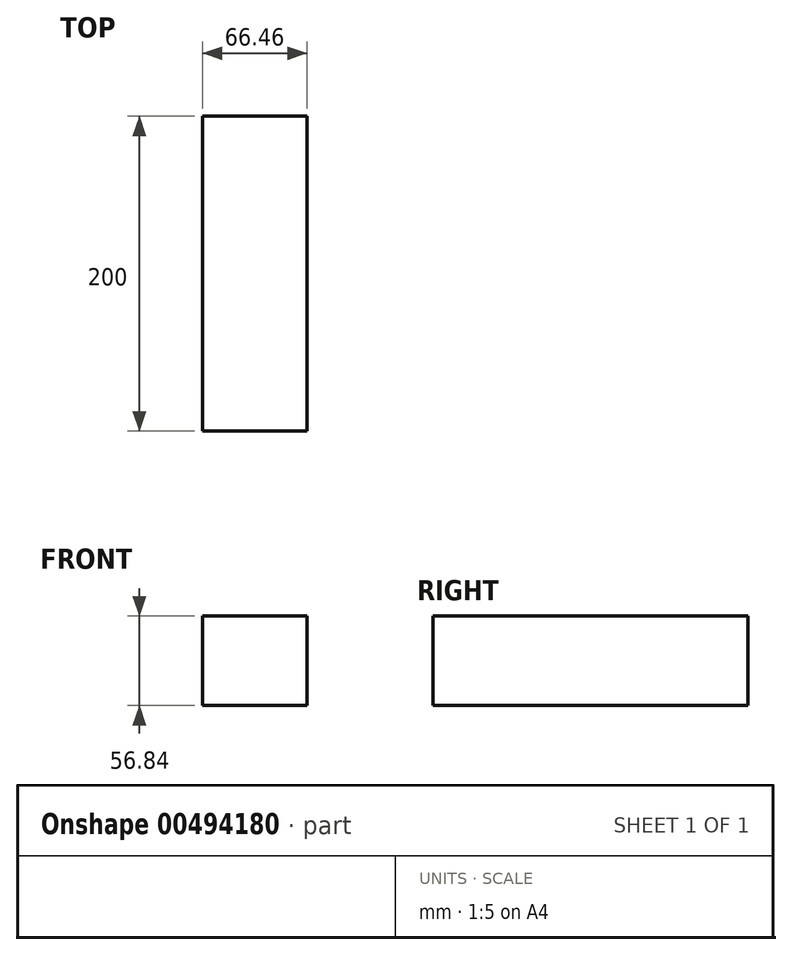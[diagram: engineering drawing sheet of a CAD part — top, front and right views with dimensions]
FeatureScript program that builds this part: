
annotation { "Feature Type Name" : "Feature", "Feature Type Description" : "" }
export const myFeature = defineFeature(function(context is Context, id is Id, definition is map)
    precondition{}
    {
        {
            var Q0;
            Q0=qCreatedBy(makeId("Front.planeOp"),FACE);
            var sketch = newSketch(context, id + "F0", { "sketchPlane" : qUnion([Q0])});
            skLineSegment(sketch, "E0.bottom", {"start": v(-33.23, 28.42) * mm, "end": v(33.23, 28.42) * mm});
            skLineSegment(sketch, "E0.top", {"start": v(-33.23, -28.42) * mm, "end": v(33.23, -28.42) * mm});
            skLineSegment(sketch, "E0.left", {"start": v(-33.23, 28.42) * mm, "end": v(-33.23, -28.42) * mm});
            skLineSegment(sketch, "E0.right", {"start": v(33.23, 28.42) * mm, "end": v(33.23, -28.42) * mm});
            skPoint(sketch, "E0.middle", {"position": v(0, 0) * mm});
            skSolve(sketch);
        }
        {
            var Q0;
            Q0=makeQuery(id+"F0.imprint","IMPRINT",FACE,{"disambiguationData":[TD([[makeQuery(id+"F0.imprint","IMPRINT",EDGE,{"derivedFrom":sQuery(id+"F0.wireOp",EDGE,"E0.bottom")}),-1.0]])]});
            extrude(context, id + "F1", {"entities" : qUnion([Q0]), "endBound" : BoundingType.SYMMETRIC, "depth" : 200 * mm});
        }
    });
